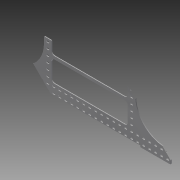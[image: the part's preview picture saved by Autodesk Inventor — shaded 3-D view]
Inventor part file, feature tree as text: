
AUTODESK INVENTOR PART (.ipt)
format: ipt  version: 2014 (Build 180170000, 170)  size: 534,528 bytes
history: native  units: in
note: dims shown in document units (in); Inventor stores cm internally (conversion verified against a paired STEP export)
features: fillet x4, extrude x2, sketch x1
ambient origin geometry x8: Origin, YZ Plane, XZ Plane, XY Plane, X Axis, Y Axis, Z Axis, Center Point
bodies: Body1 (feature_tree)
feature tree (7):
  extrude  "Extrusion2"  Depth=2.0in
  fillet  "Fillet4"  Radius=6.0in
  fillet  "Fillet5"  Radius=1.25in
  fillet  "Fillet6"  Radius=2.0in
  extrude  "Extrusion3"  Depth=2.0in
  fillet  "Fillet7"  Radius=1.25in
  sketch  "Sketch2"  dims[d0=2.0in d2=2.0in d3=6.0in d4=1.25in d5=2.0in d7=2.0in d8=1.25in d10=1.25in d11=1.25in d14=0.266in d16=0.5in d17=0.25in d32=6.5625in d33=5.9375in d34=5.9375in d75=27.125in d76=3.0in d77=3.1496in d79=1.0in d80=0.3937in d82=1.0in d84=5.5118in d86=1.0in d87=0.3937in d89=1.0in d91=1.0in d92=2.7559in d94=1.0in d95=0.3937in d97=1.0in d99=2.7559in d101=1.0in d102=0.3937in d104=1.0in d106=5.5118in d108=1.0in d109=0.3937in d111=1.0in d113=0.125in d114=0.0in d115=1.0in d116=0.125in d117=0.5in d118=1.0in d119=12.75in d120=0.25in d121=21.0in d122=3.0625in d123=0.5in d124=0.125in d125=0.0in d126=0.125in]
